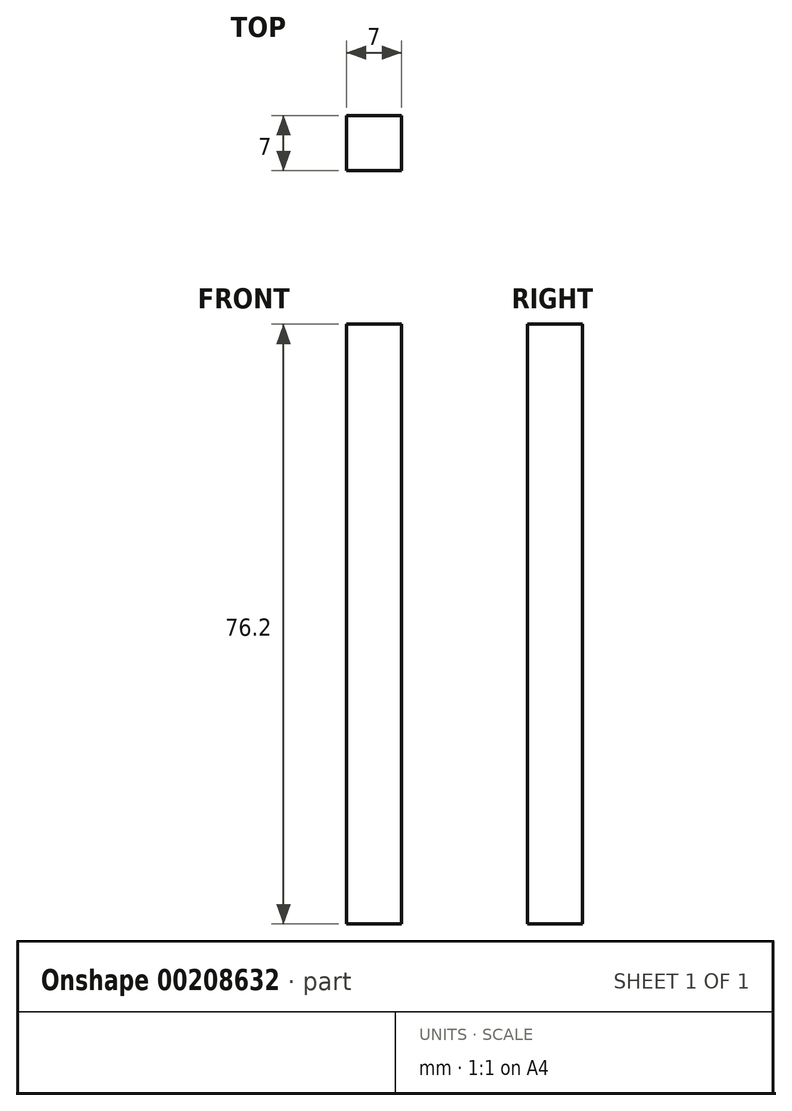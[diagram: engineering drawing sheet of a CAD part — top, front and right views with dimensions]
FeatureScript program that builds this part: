
annotation { "Feature Type Name" : "Feature", "Feature Type Description" : "" }
export const myFeature = defineFeature(function(context is Context, id is Id, definition is map)
    precondition{}
    {
        {
            var Q0;
            Q0=qCreatedBy(makeId("Top.planeOp"),FACE);
            var sketch = newSketch(context, id + "F0", { "sketchPlane" : qUnion([Q0])});
            skLineSegment(sketch, "E0.bottom", {"start": v(0.4, 6.93) * mm, "end": v(7.4, 6.93) * mm});
            skLineSegment(sketch, "E0.top", {"start": v(0.4, -0.07) * mm, "end": v(7.4, -0.07) * mm});
            skLineSegment(sketch, "E0.left", {"start": v(0.4, 6.93) * mm, "end": v(0.4, -0.07) * mm});
            skLineSegment(sketch, "E0.right", {"start": v(7.4, 6.93) * mm, "end": v(7.4, -0.07) * mm});
            skSolve(sketch);
        }
        {
            var Q0;
            Q0=makeQuery(id+"F0.imprint","IMPRINT",FACE,{"disambiguationData":[TD([[makeQuery(id+"F0.imprint","IMPRINT",EDGE,{"derivedFrom":sQuery(id+"F0.wireOp",EDGE,"E0.bottom")}),-1.0]])]});
            extrude(context, id + "F1", {"entities" : qUnion([Q0]), "depth" : 76.2 * mm});
        }
    });
